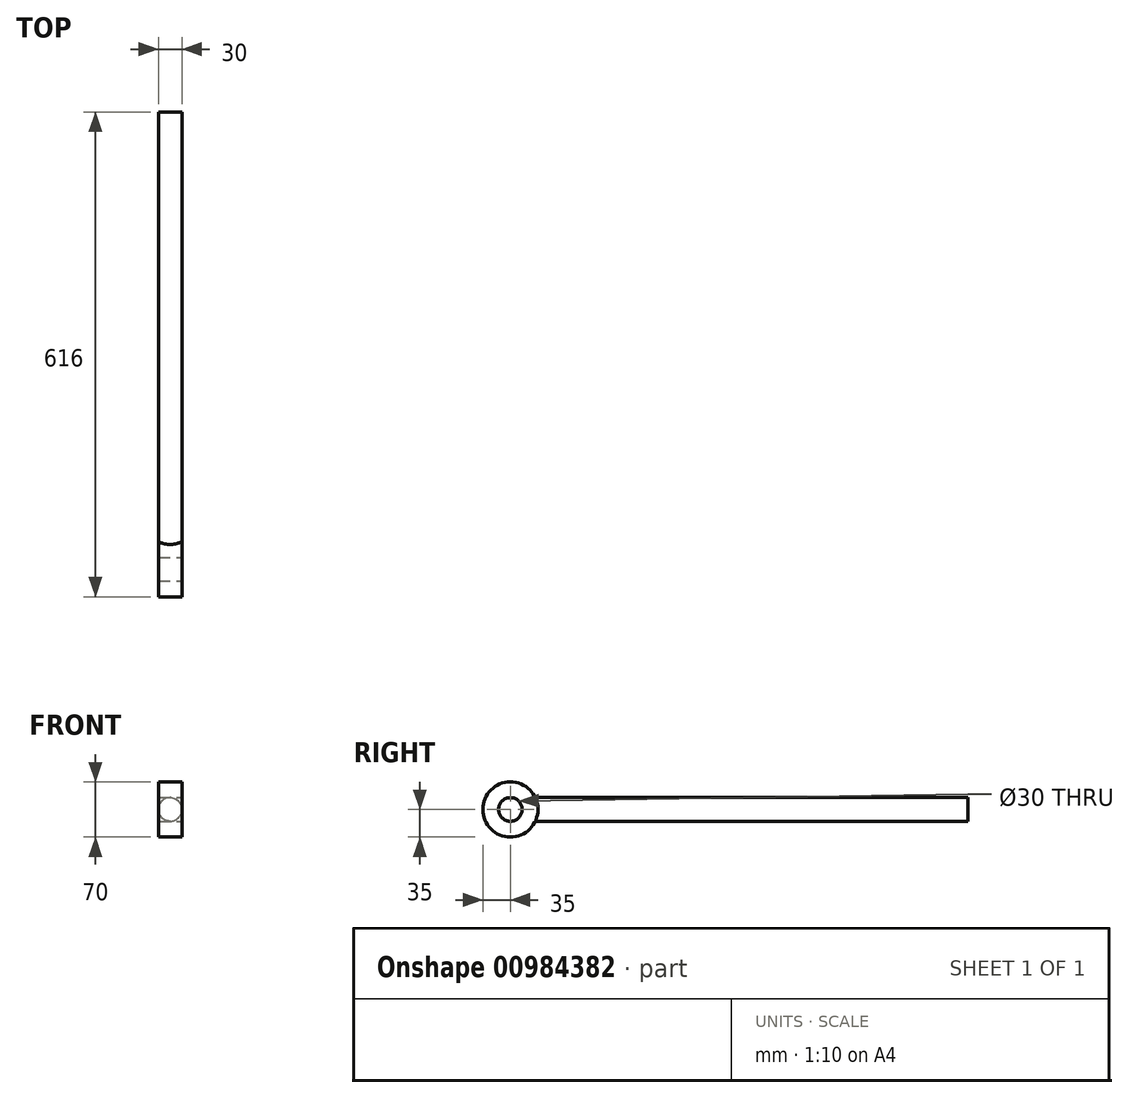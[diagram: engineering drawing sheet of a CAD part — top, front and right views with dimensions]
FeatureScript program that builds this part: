
annotation { "Feature Type Name" : "Feature", "Feature Type Description" : "" }
export const myFeature = defineFeature(function(context is Context, id is Id, definition is map)
    precondition{}
    {
        {
            var Q0;
            Q0=qCreatedBy(makeId("Front.planeOp"),FACE);
            var sketch = newSketch(context, id + "F0", { "sketchPlane" : qUnion([Q0])});
            skCircle(sketch, "E0", {"center": v(0, 0) * mm, "radius": 15 * mm});
            skSolve(sketch);
        }
        {
            var Q0;
            Q0=qSketchRegion(id+"F0",true);
            extrude(context, id + "F1", {"entities" : qUnion([Q0]), "oppositeDirection" : true, "depth" : 550 * mm, "offsetDistance" : 25 * mm});
        }
        {
            var Q0;
            Q0=qCreatedBy(makeId("Right.planeOp"),FACE);
            var sketch = newSketch(context, id + "F2", { "sketchPlane" : qUnion([Q0])});
            skCircle(sketch, "E1", {"center": v(-31, 0) * mm, "radius": 35 * mm});
            skSolve(sketch);
        }
        {
            var Q0;
            Q0=qSketchRegion(id+"F2",true);
            extrude(context, id + "F3", {"entities" : qUnion([Q0]), "operationType" : NewBodyOperationType.ADD, "depth" : 15 * mm, "offsetDistance" : 25 * mm, "hasSecondDirection" : true, "secondDirectionOppositeDirection" : true, "secondDirectionDepth" : 15 * mm});
        }
        {
            var Q0;
            Q0=makeQuery(id+"F3.opExtrude","CAP_FACE",FACE,{"disambiguationData":[OSD([sQuery(id+"F2.wireOp",EDGE,"E1")])],"isStart":false});
            var sketch = newSketch(context, id + "F4", { "sketchPlane" : qUnion([Q0])});
            skCircle(sketch, "E2", {"center": v(-31, 0) * mm, "radius": 15 * mm});
            skSolve(sketch);
        }
        {
            var Q0;
            Q0=qSketchRegion(id+"F4",true);
            extrude(context, id + "F5", {"entities" : qUnion([Q0]), "operationType" : NewBodyOperationType.REMOVE, "endBound" : BoundingType.THROUGH_ALL, "oppositeDirection" : true, "depth" : 25 * mm, "offsetDistance" : 25 * mm});
        }
    });
